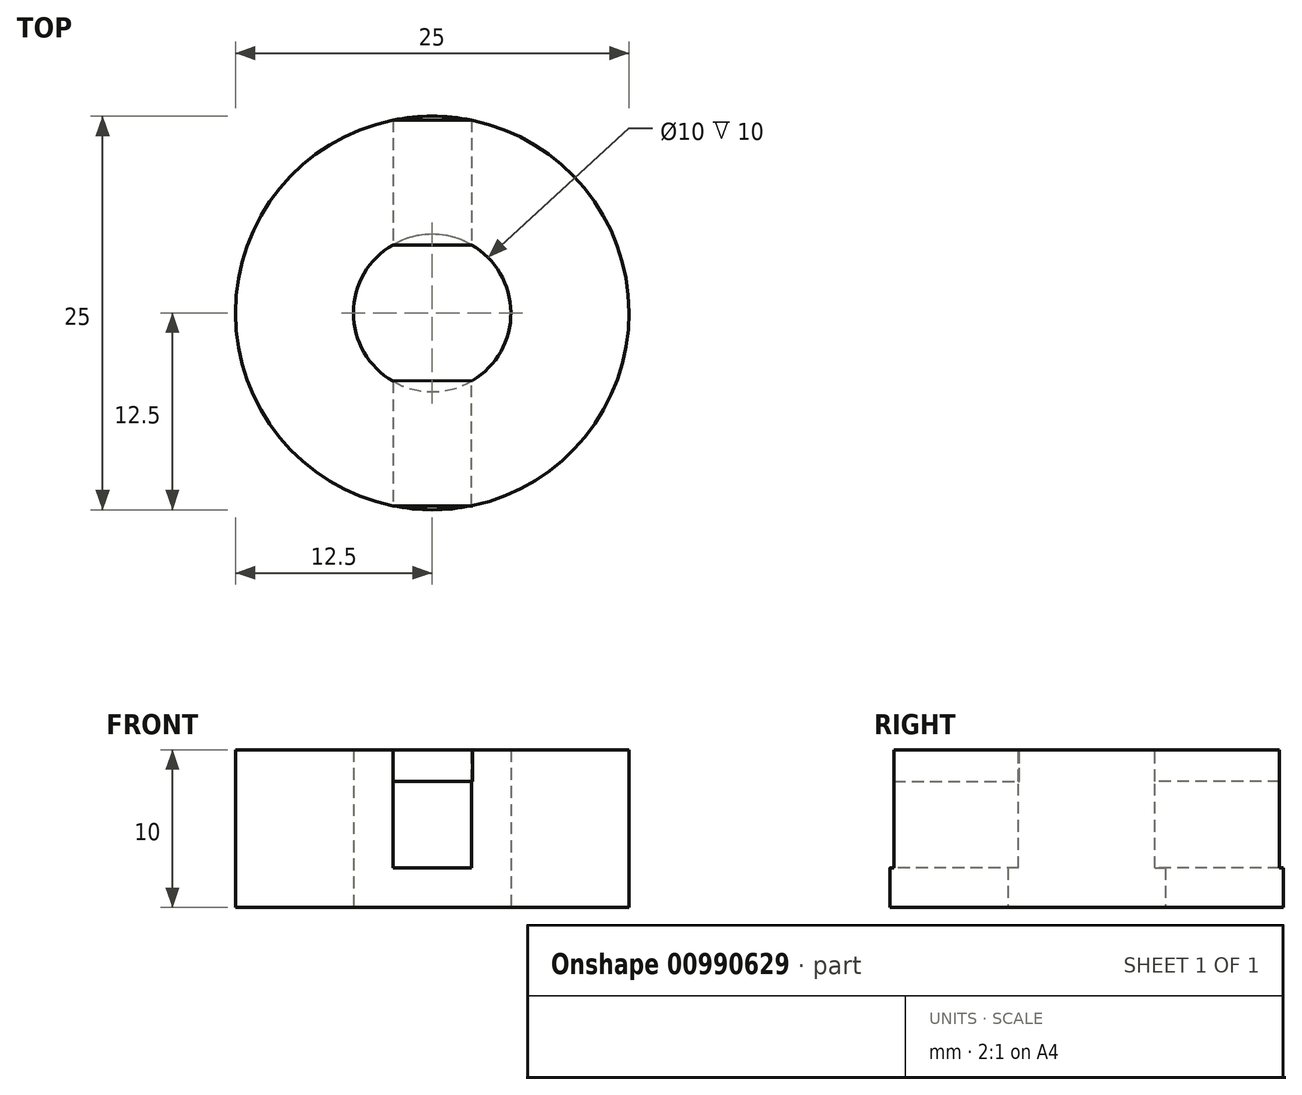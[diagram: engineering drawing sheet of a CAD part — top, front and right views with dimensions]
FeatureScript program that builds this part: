
annotation { "Feature Type Name" : "Feature", "Feature Type Description" : "" }
export const myFeature = defineFeature(function(context is Context, id is Id, definition is map)
    precondition{}
    {
        {
            var Q0;
            Q0=qCreatedBy(makeId("Top.planeOp"),FACE);
            var sketch = newSketch(context, id + "F0", { "sketchPlane" : qUnion([Q0])});
            skCircle(sketch, "E0", {"center": v(0, 0) * mm, "radius": 5 * mm});
            skCircle(sketch, "E1", {"center": v(0, 0) * mm, "radius": 12.5 * mm});
            skSolve(sketch);
        }
        {
            var Q0;
            Q0=makeQuery(id+"F0.imprint","IMPRINT",FACE,{"disambiguationData":[TD([[makeQuery(id+"F0.imprint","IMPRINT",EDGE,{"derivedFrom":sQuery(id+"F0.wireOp",EDGE,"E0")}),-1.0]])]});
            extrude(context, id + "F1", {"entities" : qUnion([Q0]), "depth" : 10 * mm, "offsetDistance" : 25 * mm});
        }
        {
            var Q0;
            Q0=makeQuery(id+"F1.opExtrude","CAP_FACE",FACE,{"disambiguationData":[OSD([sQuery(id+"F0.wireOp",EDGE,"E0"),sQuery(id+"F0.wireOp",EDGE,"E1")])],"isStart":false});
            var sketch = newSketch(context, id + "F2", { "sketchPlane" : qUnion([Q0])});
            skLineSegment(sketch, "E2", {"start": v(-2.5, 12.25) * mm, "end": v(-2.5, -12.25) * mm});
            skLineSegment(sketch, "E3", {"start": v(2.5, 12.25) * mm, "end": v(2.5, -12.25) * mm});
            skSolve(sketch);
        }
        {
            var Q0;
            {var subQ0=sQuery(id+"F2.wireOp",EDGE,"E2");var subQ1=makeQuery(id+"F1.opExtrude","CAP_EDGE",EDGE,{"disambiguationData":[OSD([sQuery(id+"F0.wireOp",EDGE,"E1")])],"isStart":false});var subQ2=makeQuery(id+"F2.imprint","INTERSECT",VERTEX,{"disambiguationData":[OD(1.0)],"derivedFrom":[subQ1,subQ0]});Q0=makeQuery(id+"F2.imprint","IMPRINT",FACE,{"disambiguationData":[TD([[makeQuery(id+"F2.imprint","IMPRINT",EDGE,{"disambiguationData":[TD([[subQ2,1.0]])],"derivedFrom":subQ0}),1.0]])]});}
            var Q1;
            {var subQ0=sQuery(id+"F2.wireOp",EDGE,"E2");var subQ1=makeQuery(id+"F1.opExtrude","CAP_EDGE",EDGE,{"disambiguationData":[OSD([sQuery(id+"F0.wireOp",EDGE,"E1")])],"isStart":false});var subQ2=makeQuery(id+"F2.imprint","INTERSECT",VERTEX,{"disambiguationData":[OD(0.0)],"derivedFrom":[subQ1,subQ0]});Q1=makeQuery(id+"F2.imprint","IMPRINT",FACE,{"disambiguationData":[TD([[makeQuery(id+"F2.imprint","IMPRINT",EDGE,{"disambiguationData":[TD([[subQ2,-1.0]])],"derivedFrom":subQ0}),1.0]])]});}
            extrude(context, id + "F3", {"entities" : qUnion([Q0, Q1]), "operationType" : NewBodyOperationType.REMOVE, "endBound" : BoundingType.SYMMETRIC, "oppositeDirection" : true, "depth" : 15 * mm, "offsetDistance" : 25 * mm});
        }
        {
            var Q0;
            {var subQ0=sQuery(id+"F0.wireOp",EDGE,"E0");var subQ1=sQuery(id+"F0.wireOp",EDGE,"E1");var subQ2=sQuery(id+"F2.wireOp",EDGE,"E2");var subQ3=makeQuery(id+"F1.opExtrude","CAP_EDGE",EDGE,{"disambiguationData":[OSD([subQ1])],"isStart":false});Q0=makeQuery(id+"F3.boolean.opBoolean","SPLIT",FACE,{"disambiguationData":[TD([makeQuery(id+"F3.opExtrude","SWEPT_FACE",FACE,{"disambiguationData":[OSD([subQ2]),TDD([makeQuery(id+"F2.imprint","IMPRINT",EDGE,{"disambiguationData":[TD([[makeQuery(id+"F2.imprint","INTERSECT",VERTEX,{"disambiguationData":[OD(0.0)],"derivedFrom":[subQ3,subQ2]}),-1.0]])],"derivedFrom":subQ2})])]})])],"derivedFrom":makeQuery(id+"F1.opExtrude","CAP_FACE",FACE,{"disambiguationData":[OSD([subQ0,subQ1])],"isStart":false})});}
            var sketch = newSketch(context, id + "F4", { "sketchPlane" : qUnion([Q0])});
            skLineSegment(sketch, "E4", {"start": v(-2.5, -12.25) * mm, "end": v(2.57, -12.25) * mm});
            skLineSegment(sketch, "E5", {"start": v(2.57, -12.25) * mm, "end": v(2.57, -4.28) * mm});
            skLineSegment(sketch, "E6", {"start": v(2.57, -4.28) * mm, "end": v(-2.5, -4.33) * mm});
            skSolve(sketch);
        }
        {
            var Q0;
            Q0=makeQuery(id+"F4.imprint","IMPRINT",FACE,{"disambiguationData":[TD([[makeQuery(id+"F4.imprint","IMPRINT",EDGE,{"derivedFrom":sQuery(id+"F4.wireOp",EDGE,"E4")}),1.0]])]});
            extrude(context, id + "F5", {"entities" : qUnion([Q0]), "operationType" : NewBodyOperationType.ADD, "oppositeDirection" : true, "depth" : 2 * mm, "offsetDistance" : 25 * mm});
        }
        {
            var Q0;
            {var subQ0=sQuery(id+"F2.wireOp",EDGE,"E2");var subQ1=sQuery(id+"F0.wireOp",EDGE,"E1");var subQ2=sQuery(id+"F0.wireOp",EDGE,"E0");var subQ4=sQuery(id+"F2.wireOp",EDGE,"E3");var subQ5=makeQuery(id+"F1.opExtrude","CAP_EDGE",EDGE,{"disambiguationData":[OSD([subQ1])],"isStart":false});var subQ8=makeQuery(id+"F1.opExtrude","CAP_FACE",FACE,{"disambiguationData":[OSD([subQ2,subQ1])],"isStart":false});Q0=makeQuery(id+"F5.boolean.opBoolean","MERGE",FACE,{"derivedFrom":[makeQuery(id+"F3.boolean.opBoolean","SPLIT",FACE,{"disambiguationData":[TD([makeQuery(id+"F3.opExtrude","SWEPT_FACE",FACE,{"disambiguationData":[OSD([subQ0]),TDD([makeQuery(id+"F2.imprint","IMPRINT",EDGE,{"disambiguationData":[TD([[makeQuery(id+"F2.imprint","INTERSECT",VERTEX,{"disambiguationData":[OD(0.0)],"derivedFrom":[subQ5,subQ0]}),-1.0]])],"derivedFrom":subQ0})])]})])],"derivedFrom":subQ8}),makeQuery(id+"F3.boolean.opBoolean","SPLIT",FACE,{"disambiguationData":[TD([makeQuery(id+"F3.opExtrude","SWEPT_FACE",FACE,{"disambiguationData":[OSD([subQ4]),TDD([makeQuery(id+"F2.imprint","IMPRINT",EDGE,{"disambiguationData":[TD([[makeQuery(id+"F2.imprint","INTERSECT",VERTEX,{"disambiguationData":[OD(0.0)],"derivedFrom":[subQ5,subQ4]}),-1.0]])],"derivedFrom":subQ4})])]})])],"derivedFrom":subQ8}),makeQuery(id+"F5.opExtrude","CAP_FACE",FACE,{"disambiguationData":[OSD([subQ2,subQ1,subQ0,sQuery(id+"F4.wireOp",EDGE,"E4"),sQuery(id+"F4.wireOp",EDGE,"E5"),sQuery(id+"F4.wireOp",EDGE,"E6")])],"isStart":true})]});}
            var sketch = newSketch(context, id + "F6", { "sketchPlane" : qUnion([Q0])});
            skLineSegment(sketch, "E7", {"start": v(-2.5, 4.33) * mm, "end": v(2.5, 4.33) * mm});
            skLineSegment(sketch, "E8", {"start": v(-2.5, 12.25) * mm, "end": v(2.5, 12.25) * mm});
            skSolve(sketch);
        }
        {
            var Q0;
            Q0=makeQuery(id+"F6.imprint","IMPRINT",FACE,{"disambiguationData":[TD([[makeQuery(id+"F6.imprint","IMPRINT",EDGE,{"derivedFrom":sQuery(id+"F6.wireOp",EDGE,"E7")}),1.0]])]});
            extrude(context, id + "F7", {"entities" : qUnion([Q0]), "operationType" : NewBodyOperationType.ADD, "oppositeDirection" : true, "depth" : 2 * mm, "offsetDistance" : 25 * mm});
        }
    });
